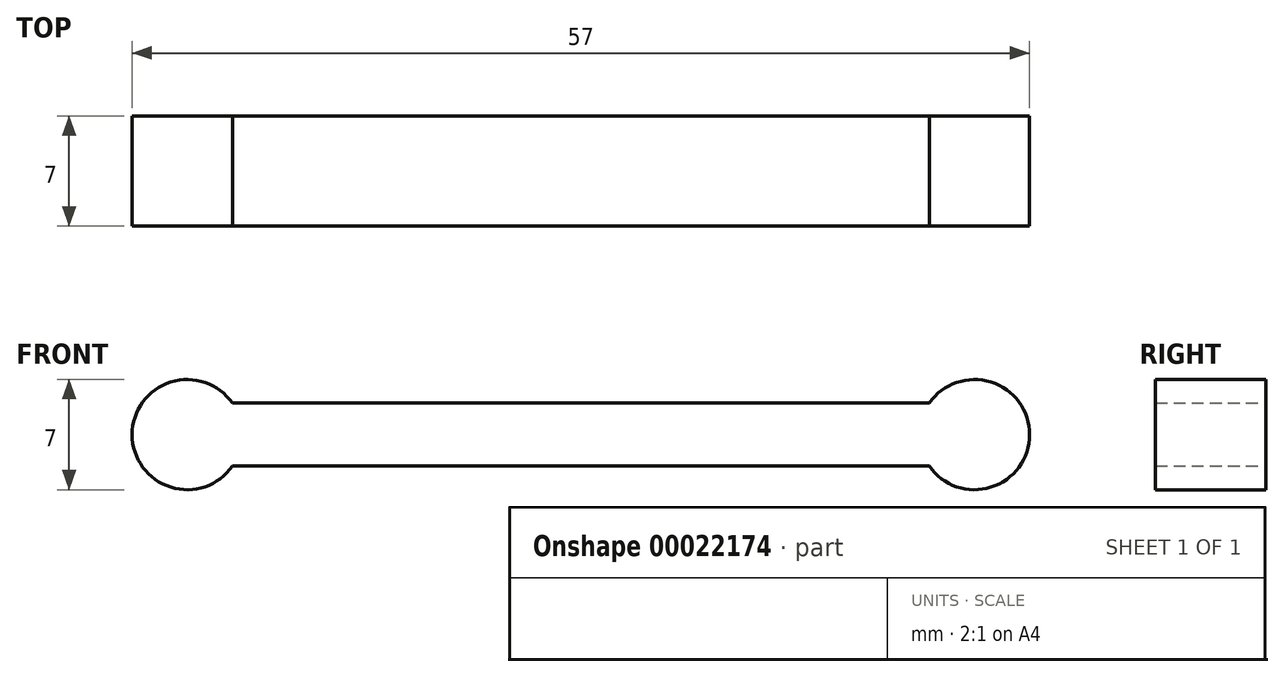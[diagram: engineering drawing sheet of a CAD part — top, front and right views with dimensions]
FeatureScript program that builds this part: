
annotation { "Feature Type Name" : "Feature", "Feature Type Description" : "" }
export const myFeature = defineFeature(function(context is Context, id is Id, definition is map)
    precondition{}
    {
        {
            var Q0;
            Q0=qCreatedBy(makeId("Front.planeOp"),FACE);
            var sketch = newSketch(context, id + "F0", { "sketchPlane" : qUnion([Q0])});
            skLineSegment(sketch, "E0.bottom", {"start": v(0, 0) * mm, "end": v(-50, 0) * mm});
            skLineSegment(sketch, "E0.top", {"start": v(0, 4) * mm, "end": v(-50, 4) * mm});
            skLineSegment(sketch, "E0.left", {"start": v(0, 0) * mm, "end": v(0, 4) * mm});
            skLineSegment(sketch, "E0.right", {"start": v(-50, 0) * mm, "end": v(-50, 4) * mm});
            skCircle(sketch, "E1", {"center": v(-50, 2) * mm, "radius": 3.5 * mm});
            skCircle(sketch, "E2", {"center": v(0, 2) * mm, "radius": 3.5 * mm});
            skSolve(sketch);
        }
        {
            var Q0;
            Q0 = qSketchRegion(id + "F0", true);
            extrude(context, id + "F1", {"entities" : qUnion([Q0]), "depth" : 7 * mm});
        }
    });
